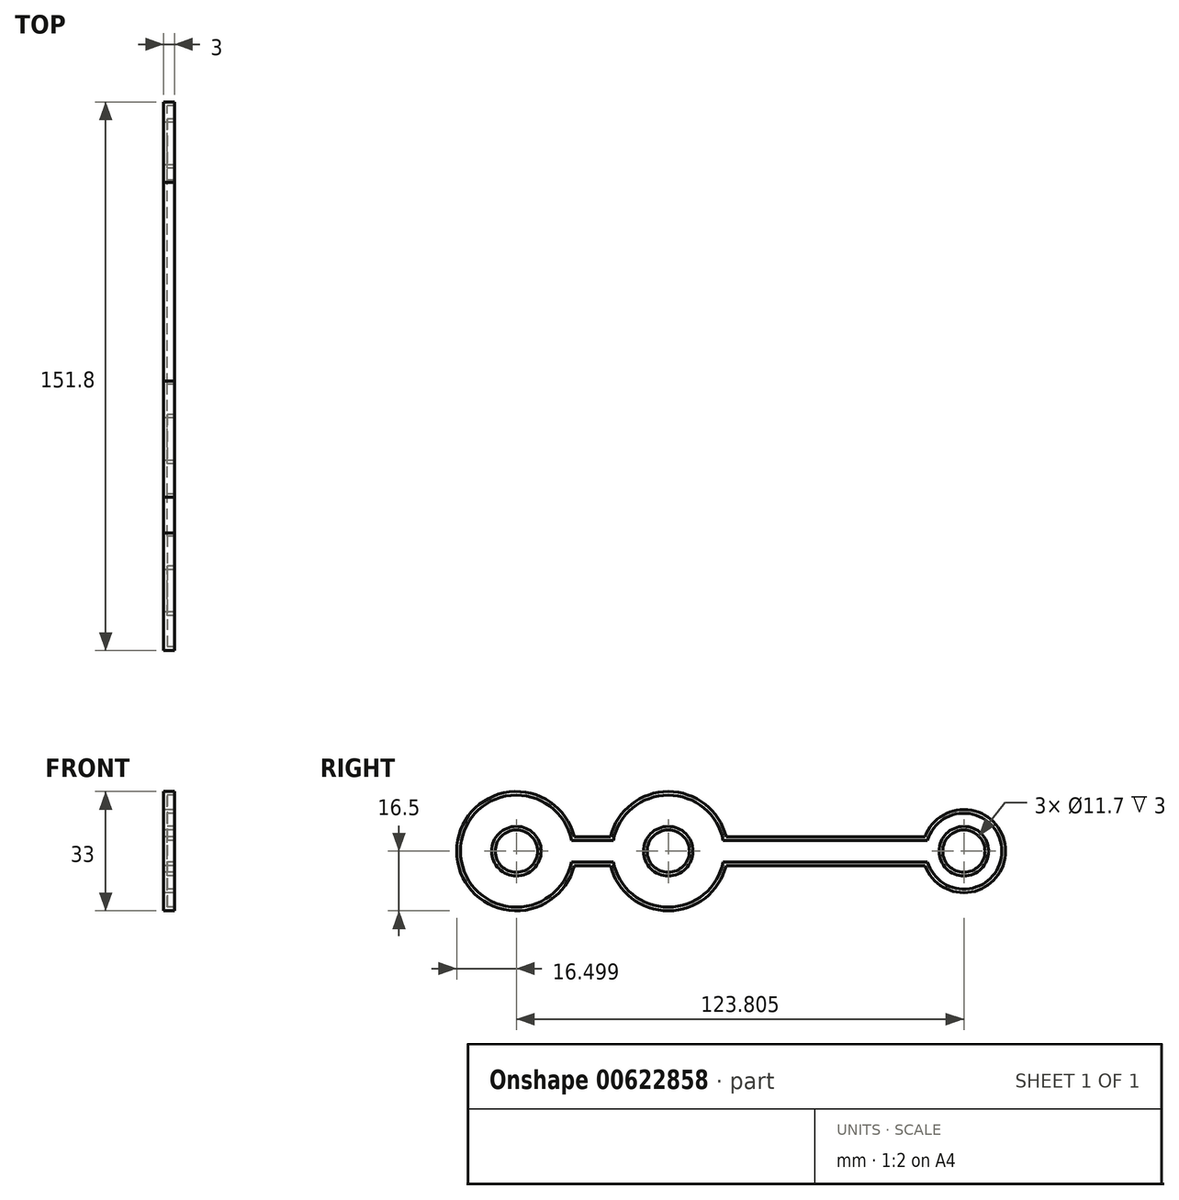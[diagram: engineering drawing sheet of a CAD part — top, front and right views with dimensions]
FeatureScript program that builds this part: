
annotation { "Feature Type Name" : "Feature", "Feature Type Description" : "" }
export const myFeature = defineFeature(function(context is Context, id is Id, definition is map)
    precondition{}
    {
        {
            var Q0;
            Q0=qCreatedBy(makeId("Right.planeOp"),FACE);
            var sketch = newSketch(context, id + "F0", { "sketchPlane" : qUnion([Q0])});
            skCircle(sketch, "E0", {"center": v(-90.92, 0) * mm, "radius": 5.85 * mm});
            skCircle(sketch, "E1", {"center": v(-90.92, 0) * mm, "radius": 16.5 * mm});
            skCircle(sketch, "E2", {"center": v(-48.9, 0) * mm, "radius": 5.85 * mm});
            skCircle(sketch, "E3", {"center": v(-48.9, 0) * mm, "radius": 16.5 * mm});
            skCircle(sketch, "E4", {"center": v(32.88, 0) * mm, "radius": 5.85 * mm});
            skCircle(sketch, "E5", {"center": v(32.88, 0) * mm, "radius": 11.5 * mm});
            skLineSegment(sketch, "E6.trimOffspring", {"start": v(-74.93, 4) * mm, "end": v(-64.88, 4) * mm});
            skLineSegment(sketch, "E7.trimOffspring", {"start": v(-74.94, -4) * mm, "end": v(-64.88, -4) * mm});
            skLineSegment(sketch, "E8.trimOffspring", {"start": v(-32.9, -4) * mm, "end": v(22.1, -4) * mm});
            skLineSegment(sketch, "E9.trimOffspring", {"start": v(-32.9, 4) * mm, "end": v(22.1, 4) * mm});
            skSolve(sketch);
        }
        {
            var Q0;
            Q0=makeQuery(id+"F0.imprint","IMPRINT",FACE,{"disambiguationData":[TD([[makeQuery(id+"F0.imprint","IMPRINT",EDGE,{"derivedFrom":sQuery(id+"F0.wireOp",EDGE,"E0")}),-1.0]])]});
            var Q1;
            {var subQ0=sQuery(id+"F0.wireOp",EDGE,"E6.trimOffspring");var subQ1=sQuery(id+"F0.wireOp",EDGE,"E1");var subQ2=makeQuery(id+"F0.imprint","INTERSECT",VERTEX,{"derivedFrom":[subQ1,subQ0]});Q1=makeQuery(id+"F0.imprint","IMPRINT",FACE,{"disambiguationData":[TD([[makeQuery(id+"F0.imprint","IMPRINT",EDGE,{"disambiguationData":[TD([[subQ2,1.0]])],"derivedFrom":subQ1}),-1.0]])]});}
            var Q2;
            Q2=makeQuery(id+"F0.imprint","IMPRINT",FACE,{"disambiguationData":[TD([[makeQuery(id+"F0.imprint","IMPRINT",EDGE,{"derivedFrom":sQuery(id+"F0.wireOp",EDGE,"E2")}),-1.0]])]});
            var Q3;
            {var subQ0=sQuery(id+"F0.wireOp",EDGE,"E8.trimOffspring");var subQ1=sQuery(id+"F0.wireOp",EDGE,"E3");var subQ2=makeQuery(id+"F0.imprint","INTERSECT",VERTEX,{"derivedFrom":[subQ1,subQ0]});Q3=makeQuery(id+"F0.imprint","IMPRINT",FACE,{"disambiguationData":[TD([[makeQuery(id+"F0.imprint","IMPRINT",EDGE,{"disambiguationData":[TD([[subQ2,-1.0]])],"derivedFrom":subQ1}),-1.0]])]});}
            var Q4;
            Q4=makeQuery(id+"F0.imprint","IMPRINT",FACE,{"disambiguationData":[TD([[makeQuery(id+"F0.imprint","IMPRINT",EDGE,{"derivedFrom":sQuery(id+"F0.wireOp",EDGE,"E4")}),-1.0]])]});
            extrude(context, id + "F1", {"entities" : qUnion([Q0, Q1, Q2, Q3, Q4]), "depth" : 3 * mm, "offsetDistance" : 25 * mm});
        }
        {
            var Q0;
            Q0=makeQuery(id+"F1.opExtrude","CAP_FACE",FACE,{"disambiguationData":[OSD([sQuery(id+"F0.wireOp",EDGE,"E0"),sQuery(id+"F0.wireOp",EDGE,"E1"),sQuery(id+"F0.wireOp",EDGE,"E2"),sQuery(id+"F0.wireOp",EDGE,"E3"),sQuery(id+"F0.wireOp",EDGE,"E4"),sQuery(id+"F0.wireOp",EDGE,"E5"),sQuery(id+"F0.wireOp",EDGE,"E6.trimOffspring"),sQuery(id+"F0.wireOp",EDGE,"E7.trimOffspring"),sQuery(id+"F0.wireOp",EDGE,"E8.trimOffspring"),sQuery(id+"F0.wireOp",EDGE,"E9.trimOffspring")])],"isStart":false});
            shell(context, id + "F2", {"entities" : qUnion([Q0]), "thickness" : 1 * mm});
        }
        {
            var Q0;
            Q0=sQuery(id+"F0.wireOp",EDGE,"E5");
            var Q1;
            Q1=sQuery(id+"F0.wireOp",EDGE,"E3");
            var Q2;
            Q2=sQuery(id+"F0.wireOp",EDGE,"E1");
            extrude(context, id + "F3", {"bodyType" : ToolBodyType.SURFACE, "surfaceEntities" : qUnion([Q0, Q1, Q2]), "oppositeDirection" : true, "depth" : 25 * mm, "offsetDistance" : 25 * mm});
        }
    });
